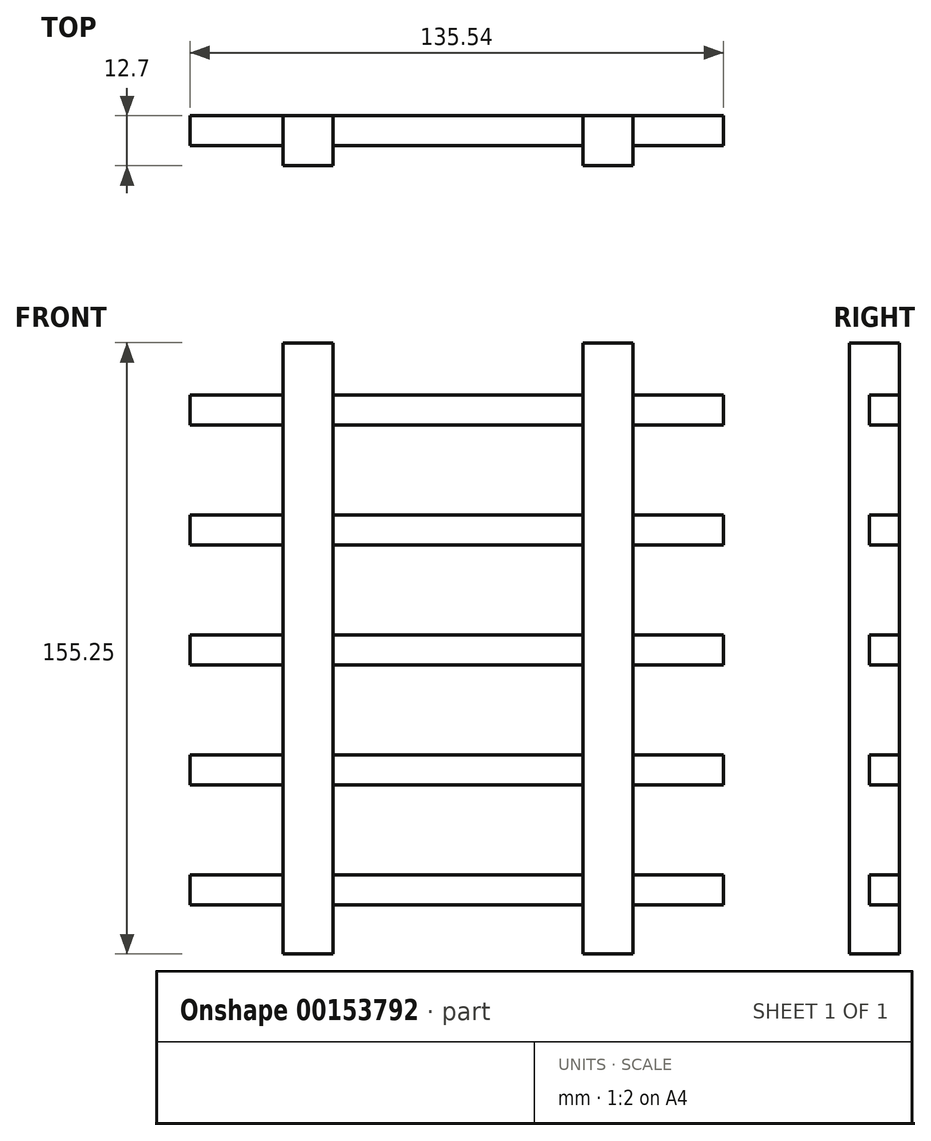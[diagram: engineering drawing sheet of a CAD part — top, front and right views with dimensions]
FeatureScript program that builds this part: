
annotation { "Feature Type Name" : "Feature", "Feature Type Description" : "" }
export const myFeature = defineFeature(function(context is Context, id is Id, definition is map)
    precondition{}
    {
        {
            var Q0;
            Q0=qCreatedBy(makeId("Front.planeOp"),FACE);
            var sketch = newSketch(context, id + "F0", { "sketchPlane" : qUnion([Q0])});
            skLineSegment(sketch, "E0", {"start": v(-35.3, -67.42) * mm, "end": v(-35.3, 74.18) * mm});
            skLineSegment(sketch, "E1", {"start": v(28.2, -67.42) * mm, "end": v(28.2, 74.18) * mm});
            skLineSegment(sketch, "E2", {"start": v(-35.3, 74.18) * mm, "end": v(-48, 74.18) * mm});
            skLineSegment(sketch, "E3", {"start": v(-48, 74.18) * mm, "end": v(-48, -67.42) * mm});
            skLineSegment(sketch, "E4", {"start": v(40.9, -67.42) * mm, "end": v(40.9, 74.18) * mm});
            skLineSegment(sketch, "E5", {"start": v(28.2, 74.18) * mm, "end": v(40.9, 74.18) * mm});
            skLineSegment(sketch, "E6", {"start": v(-71.69, 60.96) * mm, "end": v(-71.69, 53.34) * mm});
            skLineSegment(sketch, "E7", {"start": v(-71.69, 53.34) * mm, "end": v(63.85, 53.34) * mm});
            skLineSegment(sketch, "E8", {"start": v(-71.69, 60.96) * mm, "end": v(63.85, 60.96) * mm});
            skLineSegment(sketch, "E9", {"start": v(63.85, 60.96) * mm, "end": v(63.85, 53.34) * mm});
            skLineSegment(sketch, "E10", {"start": v(-71.69, 30.48) * mm, "end": v(63.85, 30.48) * mm});
            skLineSegment(sketch, "E11", {"start": v(-71.69, 30.48) * mm, "end": v(-71.69, 22.86) * mm});
            skLineSegment(sketch, "E12", {"start": v(-71.69, 22.86) * mm, "end": v(63.85, 22.86) * mm});
            skLineSegment(sketch, "E13", {"start": v(63.85, 30.48) * mm, "end": v(63.85, 22.86) * mm});
            skLineSegment(sketch, "E14", {"start": v(-71.69, 0) * mm, "end": v(63.85, 0) * mm});
            skLineSegment(sketch, "E15", {"start": v(-71.69, 0) * mm, "end": v(-71.69, -7.62) * mm});
            skLineSegment(sketch, "E16", {"start": v(-71.69, -7.62) * mm, "end": v(63.85, -7.62) * mm});
            skLineSegment(sketch, "E17", {"start": v(63.85, 0) * mm, "end": v(63.85, -7.62) * mm});
            skLineSegment(sketch, "E18", {"start": v(-71.69, -30.48) * mm, "end": v(63.85, -30.48) * mm});
            skLineSegment(sketch, "E19", {"start": v(63.85, -30.48) * mm, "end": v(63.85, -38.1) * mm});
            skLineSegment(sketch, "E20", {"start": v(63.85, -38.1) * mm, "end": v(-71.69, -38.1) * mm});
            skLineSegment(sketch, "E21", {"start": v(-71.69, -38.1) * mm, "end": v(-71.69, -30.48) * mm});
            skLineSegment(sketch, "E22", {"start": v(-71.69, -60.96) * mm, "end": v(63.85, -60.96) * mm});
            skLineSegment(sketch, "E23", {"start": v(63.85, -60.96) * mm, "end": v(63.85, -68.58) * mm});
            skLineSegment(sketch, "E24", {"start": v(63.85, -68.58) * mm, "end": v(-71.69, -68.58) * mm});
            skLineSegment(sketch, "E25", {"start": v(-71.69, -68.58) * mm, "end": v(-71.69, -60.96) * mm});
            skLineSegment(sketch, "E26", {"start": v(28.2, -67.42) * mm, "end": v(28.2, -81.07) * mm});
            skLineSegment(sketch, "E27", {"start": v(28.2, -81.07) * mm, "end": v(40.9, -81.07) * mm});
            skLineSegment(sketch, "E28", {"start": v(40.9, -81.07) * mm, "end": v(40.9, -67.42) * mm});
            skLineSegment(sketch, "E29", {"start": v(-48, -67.42) * mm, "end": v(-48, -81.07) * mm});
            skLineSegment(sketch, "E30", {"start": v(-48, -81.07) * mm, "end": v(-35.3, -81.07) * mm});
            skLineSegment(sketch, "E31", {"start": v(-35.3, -81.07) * mm, "end": v(-35.3, -67.42) * mm});
            skSolve(sketch);
        }
        {
            var Q0;
            {var subQ0=sQuery(id+"F0.wireOp",EDGE,"E2");Q0=makeQuery(id+"F0.imprint","IMPRINT",FACE,{"disambiguationData":[TD([[makeQuery(id+"F0.imprint","IMPRINT",EDGE,{"derivedFrom":subQ0}),1.0]])]});}
            var Q1;
            {var subQ0=sQuery(id+"F0.wireOp",EDGE,"E5");Q1=makeQuery(id+"F0.imprint","IMPRINT",FACE,{"disambiguationData":[TD([[makeQuery(id+"F0.imprint","IMPRINT",EDGE,{"derivedFrom":subQ0}),-1.0]])]});}
            var Q2;
            {var subQ0=sQuery(id+"F0.wireOp",EDGE,"E10");var subQ1=sQuery(id+"F0.wireOp",EDGE,"E1");var subQ2=makeQuery(id+"F0.imprint","INTERSECT",VERTEX,{"derivedFrom":[subQ1,subQ0]});Q2=makeQuery(id+"F0.imprint","IMPRINT",FACE,{"disambiguationData":[TD([[makeQuery(id+"F0.imprint","IMPRINT",EDGE,{"disambiguationData":[TD([[subQ2,-1.0]])],"derivedFrom":subQ1}),-1.0]])]});}
            var Q3;
            {var subQ0=sQuery(id+"F0.wireOp",EDGE,"E10");var subQ1=sQuery(id+"F0.wireOp",EDGE,"E0");var subQ2=makeQuery(id+"F0.imprint","INTERSECT",VERTEX,{"derivedFrom":[subQ1,subQ0]});Q3=makeQuery(id+"F0.imprint","IMPRINT",FACE,{"disambiguationData":[TD([[makeQuery(id+"F0.imprint","IMPRINT",EDGE,{"disambiguationData":[TD([[subQ2,-1.0]])],"derivedFrom":subQ1}),1.0]])]});}
            var Q4;
            {var subQ0=sQuery(id+"F0.wireOp",EDGE,"E14");var subQ1=sQuery(id+"F0.wireOp",EDGE,"E1");var subQ2=makeQuery(id+"F0.imprint","INTERSECT",VERTEX,{"derivedFrom":[subQ1,subQ0]});Q4=makeQuery(id+"F0.imprint","IMPRINT",FACE,{"disambiguationData":[TD([[makeQuery(id+"F0.imprint","IMPRINT",EDGE,{"disambiguationData":[TD([[subQ2,-1.0]])],"derivedFrom":subQ1}),-1.0]])]});}
            var Q5;
            {var subQ0=sQuery(id+"F0.wireOp",EDGE,"E14");var subQ1=sQuery(id+"F0.wireOp",EDGE,"E0");var subQ2=makeQuery(id+"F0.imprint","INTERSECT",VERTEX,{"derivedFrom":[subQ1,subQ0]});Q5=makeQuery(id+"F0.imprint","IMPRINT",FACE,{"disambiguationData":[TD([[makeQuery(id+"F0.imprint","IMPRINT",EDGE,{"disambiguationData":[TD([[subQ2,-1.0]])],"derivedFrom":subQ1}),1.0]])]});}
            var Q6;
            {var subQ0=sQuery(id+"F0.wireOp",EDGE,"E18");var subQ1=sQuery(id+"F0.wireOp",EDGE,"E0");var subQ2=makeQuery(id+"F0.imprint","INTERSECT",VERTEX,{"derivedFrom":[subQ1,subQ0]});Q6=makeQuery(id+"F0.imprint","IMPRINT",FACE,{"disambiguationData":[TD([[makeQuery(id+"F0.imprint","IMPRINT",EDGE,{"disambiguationData":[TD([[subQ2,-1.0]])],"derivedFrom":subQ1}),1.0]])]});}
            var Q7;
            {var subQ0=sQuery(id+"F0.wireOp",EDGE,"E18");var subQ1=sQuery(id+"F0.wireOp",EDGE,"E1");var subQ2=makeQuery(id+"F0.imprint","INTERSECT",VERTEX,{"derivedFrom":[subQ1,subQ0]});Q7=makeQuery(id+"F0.imprint","IMPRINT",FACE,{"disambiguationData":[TD([[makeQuery(id+"F0.imprint","IMPRINT",EDGE,{"disambiguationData":[TD([[subQ2,-1.0]])],"derivedFrom":subQ1}),-1.0]])]});}
            var Q8;
            {var subQ0=sQuery(id+"F0.wireOp",EDGE,"E22");var subQ1=sQuery(id+"F0.wireOp",EDGE,"E1");var subQ2=makeQuery(id+"F0.imprint","INTERSECT",VERTEX,{"derivedFrom":[subQ1,subQ0]});Q8=makeQuery(id+"F0.imprint","IMPRINT",FACE,{"disambiguationData":[TD([[makeQuery(id+"F0.imprint","IMPRINT",EDGE,{"disambiguationData":[TD([[subQ2,-1.0]])],"derivedFrom":subQ1}),-1.0]])]});}
            var Q9;
            {var subQ0=sQuery(id+"F0.wireOp",EDGE,"E22");var subQ1=sQuery(id+"F0.wireOp",EDGE,"E0");var subQ2=makeQuery(id+"F0.imprint","INTERSECT",VERTEX,{"derivedFrom":[subQ1,subQ0]});Q9=makeQuery(id+"F0.imprint","IMPRINT",FACE,{"disambiguationData":[TD([[makeQuery(id+"F0.imprint","IMPRINT",EDGE,{"disambiguationData":[TD([[subQ2,-1.0]])],"derivedFrom":subQ1}),1.0]])]});}
            var Q10;
            {var subQ5=sQuery(id+"F0.wireOp",EDGE,"E27");Q10=makeQuery(id+"F0.imprint","IMPRINT",FACE,{"disambiguationData":[TD([[makeQuery(id+"F0.imprint","IMPRINT",EDGE,{"derivedFrom":subQ5}),1.0]])]});}
            var Q11;
            {var subQ5=sQuery(id+"F0.wireOp",EDGE,"E30");Q11=makeQuery(id+"F0.imprint","IMPRINT",FACE,{"disambiguationData":[TD([[makeQuery(id+"F0.imprint","IMPRINT",EDGE,{"derivedFrom":subQ5}),1.0]])]});}
            var Q12;
            {var subQ0=sQuery(id+"F0.wireOp",EDGE,"E8");var subQ1=sQuery(id+"F0.wireOp",EDGE,"E0");var subQ2=makeQuery(id+"F0.imprint","INTERSECT",VERTEX,{"derivedFrom":[subQ1,subQ0]});Q12=makeQuery(id+"F0.imprint","IMPRINT",FACE,{"disambiguationData":[TD([[makeQuery(id+"F0.imprint","IMPRINT",EDGE,{"disambiguationData":[TD([[subQ2,1.0]])],"derivedFrom":subQ1}),1.0]])]});}
            var Q13;
            {var subQ0=sQuery(id+"F0.wireOp",EDGE,"E8");var subQ1=sQuery(id+"F0.wireOp",EDGE,"E1");var subQ2=makeQuery(id+"F0.imprint","INTERSECT",VERTEX,{"derivedFrom":[subQ1,subQ0]});Q13=makeQuery(id+"F0.imprint","IMPRINT",FACE,{"disambiguationData":[TD([[makeQuery(id+"F0.imprint","IMPRINT",EDGE,{"disambiguationData":[TD([[subQ2,1.0]])],"derivedFrom":subQ1}),-1.0]])]});}
            var Q14;
            {var subQ0=sQuery(id+"F0.wireOp",EDGE,"E12");var subQ1=sQuery(id+"F0.wireOp",EDGE,"E1");var subQ2=makeQuery(id+"F0.imprint","INTERSECT",VERTEX,{"derivedFrom":[subQ1,subQ0]});Q14=makeQuery(id+"F0.imprint","IMPRINT",FACE,{"disambiguationData":[TD([[makeQuery(id+"F0.imprint","IMPRINT",EDGE,{"disambiguationData":[TD([[subQ2,-1.0]])],"derivedFrom":subQ1}),-1.0]])]});}
            var Q15;
            {var subQ0=sQuery(id+"F0.wireOp",EDGE,"E16");var subQ1=sQuery(id+"F0.wireOp",EDGE,"E1");var subQ2=makeQuery(id+"F0.imprint","INTERSECT",VERTEX,{"derivedFrom":[subQ1,subQ0]});Q15=makeQuery(id+"F0.imprint","IMPRINT",FACE,{"disambiguationData":[TD([[makeQuery(id+"F0.imprint","IMPRINT",EDGE,{"disambiguationData":[TD([[subQ2,-1.0]])],"derivedFrom":subQ1}),-1.0]])]});}
            var Q16;
            {var subQ0=sQuery(id+"F0.wireOp",EDGE,"E20");var subQ1=sQuery(id+"F0.wireOp",EDGE,"E1");var subQ2=makeQuery(id+"F0.imprint","INTERSECT",VERTEX,{"derivedFrom":[subQ1,subQ0]});Q16=makeQuery(id+"F0.imprint","IMPRINT",FACE,{"disambiguationData":[TD([[makeQuery(id+"F0.imprint","IMPRINT",EDGE,{"disambiguationData":[TD([[subQ2,-1.0]])],"derivedFrom":subQ1}),-1.0]])]});}
            var Q17;
            {var subQ3=sQuery(id+"F0.wireOp",EDGE,"E26");var subQ8=sQuery(id+"F0.wireOp",EDGE,"E1");var subQ11=makeQuery(id+"F0.imprint","INTERSECT",VERTEX,{"derivedFrom":[subQ8,subQ3]});Q17=makeQuery(id+"F0.imprint","IMPRINT",FACE,{"disambiguationData":[TD([[makeQuery(id+"F0.imprint","IMPRINT",EDGE,{"disambiguationData":[TD([[subQ11,-1.0]])],"derivedFrom":subQ8}),-1.0]])]});}
            var Q18;
            {var subQ3=sQuery(id+"F0.wireOp",EDGE,"E0");var subQ5=sQuery(id+"F0.wireOp",EDGE,"E31");var subQ6=makeQuery(id+"F0.imprint","INTERSECT",VERTEX,{"derivedFrom":[subQ3,subQ5]});Q18=makeQuery(id+"F0.imprint","IMPRINT",FACE,{"disambiguationData":[TD([[makeQuery(id+"F0.imprint","IMPRINT",EDGE,{"disambiguationData":[TD([[subQ6,-1.0]])],"derivedFrom":subQ3}),1.0]])]});}
            var Q19;
            {var subQ0=sQuery(id+"F0.wireOp",EDGE,"E20");var subQ1=sQuery(id+"F0.wireOp",EDGE,"E0");var subQ2=makeQuery(id+"F0.imprint","INTERSECT",VERTEX,{"derivedFrom":[subQ1,subQ0]});Q19=makeQuery(id+"F0.imprint","IMPRINT",FACE,{"disambiguationData":[TD([[makeQuery(id+"F0.imprint","IMPRINT",EDGE,{"disambiguationData":[TD([[subQ2,-1.0]])],"derivedFrom":subQ1}),1.0]])]});}
            var Q20;
            {var subQ0=sQuery(id+"F0.wireOp",EDGE,"E16");var subQ1=sQuery(id+"F0.wireOp",EDGE,"E0");var subQ2=makeQuery(id+"F0.imprint","INTERSECT",VERTEX,{"derivedFrom":[subQ1,subQ0]});Q20=makeQuery(id+"F0.imprint","IMPRINT",FACE,{"disambiguationData":[TD([[makeQuery(id+"F0.imprint","IMPRINT",EDGE,{"disambiguationData":[TD([[subQ2,-1.0]])],"derivedFrom":subQ1}),1.0]])]});}
            var Q21;
            {var subQ0=sQuery(id+"F0.wireOp",EDGE,"E12");var subQ1=sQuery(id+"F0.wireOp",EDGE,"E0");var subQ2=makeQuery(id+"F0.imprint","INTERSECT",VERTEX,{"derivedFrom":[subQ1,subQ0]});Q21=makeQuery(id+"F0.imprint","IMPRINT",FACE,{"disambiguationData":[TD([[makeQuery(id+"F0.imprint","IMPRINT",EDGE,{"disambiguationData":[TD([[subQ2,-1.0]])],"derivedFrom":subQ1}),1.0]])]});}
            extrude(context, id + "F1", {"entities" : qUnion([Q0, Q1, Q2, Q3, Q4, Q5, Q6, Q7, Q8, Q9, Q10, Q11, Q12, Q13, Q14, Q15, Q16, Q17, Q18, Q19, Q20, Q21]), "depth" : 12.7 * mm});
        }
        {
            var Q0;
            {var subQ5=sQuery(id+"F0.wireOp",EDGE,"E6");Q0=makeQuery(id+"F0.imprint","IMPRINT",FACE,{"disambiguationData":[TD([[makeQuery(id+"F0.imprint","IMPRINT",EDGE,{"derivedFrom":subQ5}),1.0]])]});}
            var Q1;
            {var subQ0=sQuery(id+"F0.wireOp",EDGE,"E8");var subQ1=sQuery(id+"F0.wireOp",EDGE,"E0");var subQ2=makeQuery(id+"F0.imprint","INTERSECT",VERTEX,{"derivedFrom":[subQ1,subQ0]});Q1=makeQuery(id+"F0.imprint","IMPRINT",FACE,{"disambiguationData":[TD([[makeQuery(id+"F0.imprint","IMPRINT",EDGE,{"disambiguationData":[TD([[subQ2,1.0]])],"derivedFrom":subQ1}),-1.0]])]});}
            var Q2;
            {var subQ5=sQuery(id+"F0.wireOp",EDGE,"E11");Q2=makeQuery(id+"F0.imprint","IMPRINT",FACE,{"disambiguationData":[TD([[makeQuery(id+"F0.imprint","IMPRINT",EDGE,{"derivedFrom":subQ5}),1.0]])]});}
            var Q3;
            {var subQ0=sQuery(id+"F0.wireOp",EDGE,"E12");var subQ1=sQuery(id+"F0.wireOp",EDGE,"E0");var subQ2=makeQuery(id+"F0.imprint","INTERSECT",VERTEX,{"derivedFrom":[subQ1,subQ0]});Q3=makeQuery(id+"F0.imprint","IMPRINT",FACE,{"disambiguationData":[TD([[makeQuery(id+"F0.imprint","IMPRINT",EDGE,{"disambiguationData":[TD([[subQ2,-1.0]])],"derivedFrom":subQ1}),-1.0]])]});}
            var Q4;
            {var subQ5=sQuery(id+"F0.wireOp",EDGE,"E15");Q4=makeQuery(id+"F0.imprint","IMPRINT",FACE,{"disambiguationData":[TD([[makeQuery(id+"F0.imprint","IMPRINT",EDGE,{"derivedFrom":subQ5}),1.0]])]});}
            var Q5;
            {var subQ0=sQuery(id+"F0.wireOp",EDGE,"E16");var subQ1=sQuery(id+"F0.wireOp",EDGE,"E0");var subQ2=makeQuery(id+"F0.imprint","INTERSECT",VERTEX,{"derivedFrom":[subQ1,subQ0]});Q5=makeQuery(id+"F0.imprint","IMPRINT",FACE,{"disambiguationData":[TD([[makeQuery(id+"F0.imprint","IMPRINT",EDGE,{"disambiguationData":[TD([[subQ2,-1.0]])],"derivedFrom":subQ1}),-1.0]])]});}
            var Q6;
            {var subQ5=sQuery(id+"F0.wireOp",EDGE,"E21");Q6=makeQuery(id+"F0.imprint","IMPRINT",FACE,{"disambiguationData":[TD([[makeQuery(id+"F0.imprint","IMPRINT",EDGE,{"derivedFrom":subQ5}),-1.0]])]});}
            var Q7;
            {var subQ0=sQuery(id+"F0.wireOp",EDGE,"E20");var subQ1=sQuery(id+"F0.wireOp",EDGE,"E0");var subQ2=makeQuery(id+"F0.imprint","INTERSECT",VERTEX,{"derivedFrom":[subQ1,subQ0]});Q7=makeQuery(id+"F0.imprint","IMPRINT",FACE,{"disambiguationData":[TD([[makeQuery(id+"F0.imprint","IMPRINT",EDGE,{"disambiguationData":[TD([[subQ2,-1.0]])],"derivedFrom":subQ1}),-1.0]])]});}
            var Q8;
            {var subQ0=sQuery(id+"F0.wireOp",EDGE,"E25");Q8=makeQuery(id+"F0.imprint","IMPRINT",FACE,{"disambiguationData":[TD([[makeQuery(id+"F0.imprint","IMPRINT",EDGE,{"derivedFrom":subQ0}),-1.0]])]});}
            var Q9;
            {var subQ1=sQuery(id+"F0.wireOp",EDGE,"E0");var subQ9=sQuery(id+"F0.wireOp",EDGE,"E31");var subQ11=makeQuery(id+"F0.imprint","INTERSECT",VERTEX,{"derivedFrom":[subQ1,subQ9]});Q9=makeQuery(id+"F0.imprint","IMPRINT",FACE,{"disambiguationData":[TD([[makeQuery(id+"F0.imprint","IMPRINT",EDGE,{"disambiguationData":[TD([[subQ11,-1.0]])],"derivedFrom":subQ1}),-1.0]])]});}
            var Q10;
            {var subQ1=sQuery(id+"F0.wireOp",EDGE,"E23");Q10=makeQuery(id+"F0.imprint","IMPRINT",FACE,{"disambiguationData":[TD([[makeQuery(id+"F0.imprint","IMPRINT",EDGE,{"derivedFrom":subQ1}),-1.0]])]});}
            var Q11;
            {var subQ5=sQuery(id+"F0.wireOp",EDGE,"E19");Q11=makeQuery(id+"F0.imprint","IMPRINT",FACE,{"disambiguationData":[TD([[makeQuery(id+"F0.imprint","IMPRINT",EDGE,{"derivedFrom":subQ5}),-1.0]])]});}
            var Q12;
            {var subQ5=sQuery(id+"F0.wireOp",EDGE,"E17");Q12=makeQuery(id+"F0.imprint","IMPRINT",FACE,{"disambiguationData":[TD([[makeQuery(id+"F0.imprint","IMPRINT",EDGE,{"derivedFrom":subQ5}),-1.0]])]});}
            var Q13;
            {var subQ5=sQuery(id+"F0.wireOp",EDGE,"E13");Q13=makeQuery(id+"F0.imprint","IMPRINT",FACE,{"disambiguationData":[TD([[makeQuery(id+"F0.imprint","IMPRINT",EDGE,{"derivedFrom":subQ5}),-1.0]])]});}
            var Q14;
            {var subQ5=sQuery(id+"F0.wireOp",EDGE,"E9");Q14=makeQuery(id+"F0.imprint","IMPRINT",FACE,{"disambiguationData":[TD([[makeQuery(id+"F0.imprint","IMPRINT",EDGE,{"derivedFrom":subQ5}),-1.0]])]});}
            extrude(context, id + "F2", {"entities" : qUnion([Q0, Q1, Q2, Q3, Q4, Q5, Q6, Q7, Q8, Q9, Q10, Q11, Q12, Q13, Q14]), "depth" : 7.62 * mm});
        }
    });
